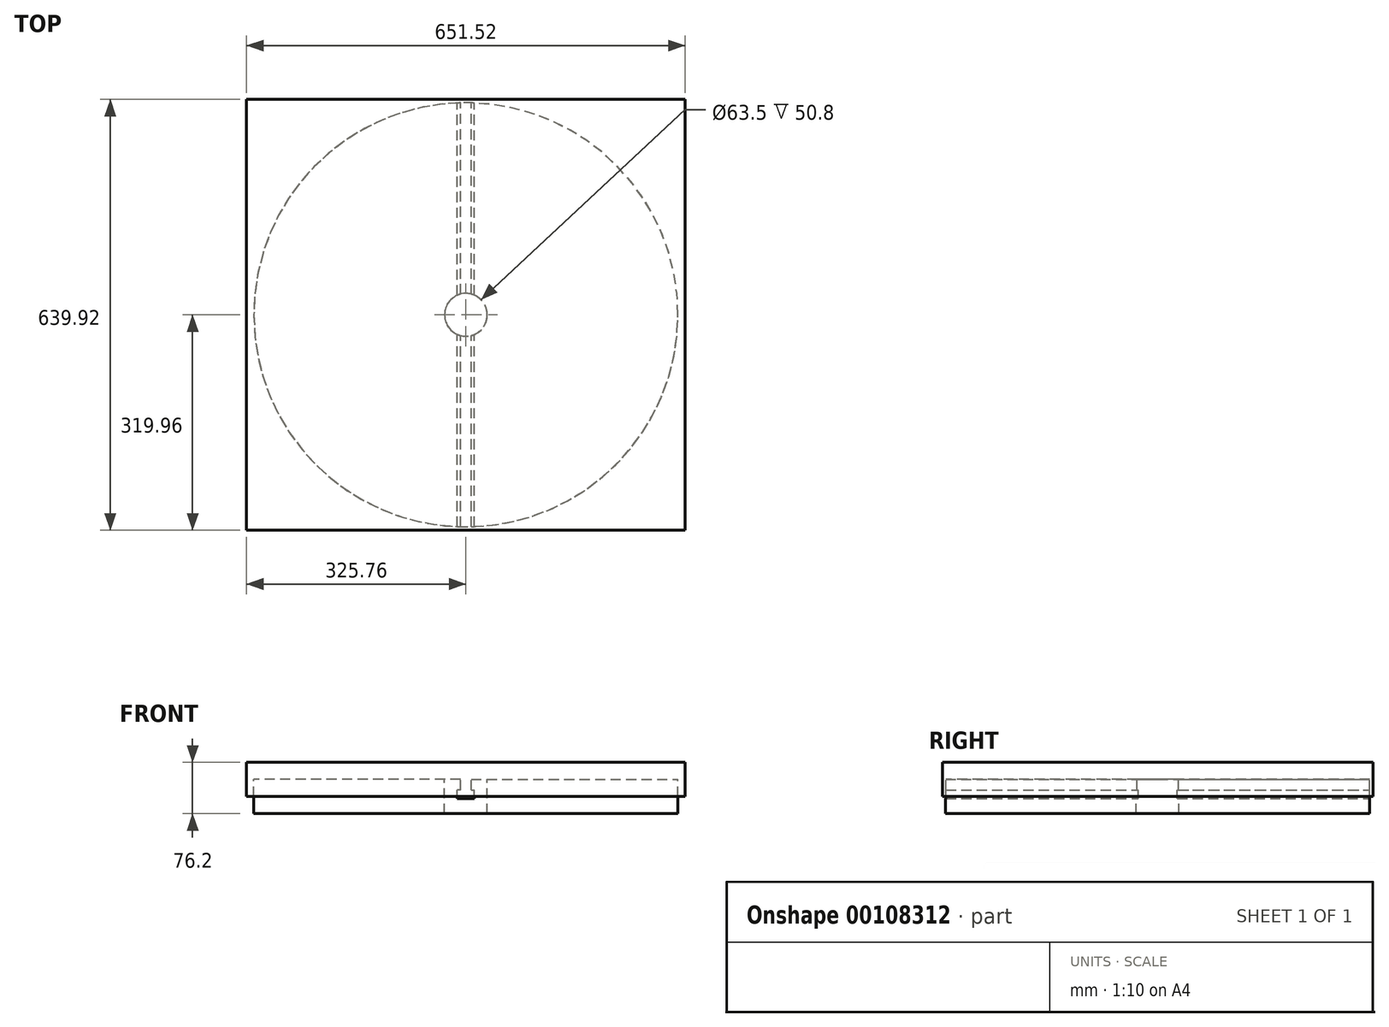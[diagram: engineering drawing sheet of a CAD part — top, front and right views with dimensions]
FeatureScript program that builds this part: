
annotation { "Feature Type Name" : "Feature", "Feature Type Description" : "" }
export const myFeature = defineFeature(function(context is Context, id is Id, definition is map)
    precondition{}
    {
        {
            var Q0;
            Q0=qCreatedBy(makeId("Top.planeOp"),FACE);
            var sketch = newSketch(context, id + "F0", { "sketchPlane" : qUnion([Q0])});
            skCircle(sketch, "E0", {"center": v(0, 0) * mm, "radius": 314.96 * mm});
            skCircle(sketch, "E1", {"center": v(0, 0) * mm, "radius": 31.75 * mm});
            skSolve(sketch);
        }
        {
            var Q0;
            Q0 = qSketchRegion(id + "F0", true);
            extrude(context, id + "F1", {"entities" : qUnion([Q0]), "oppositeDirection" : true, "depth" : 101.6 * mm, "hasSecondDirection" : true, "secondDirectionOppositeDirection" : true, "secondDirectionDepth" : 50.8 * mm});
        }
        {
            var Q0;
            Q0=qCreatedBy(makeId("Front.planeOp"),FACE);
            var sketch = newSketch(context, id + "F2", { "sketchPlane" : qUnion([Q0])});
            skLineSegment(sketch, "E2", {"start": v(0, -90) * mm, "end": v(0, -167.35) * mm, "construction": true});
            skLineSegment(sketch, "E3", {"start": v(0, -50.8) * mm, "end": v(-7.94, -50.8) * mm});
            skLineSegment(sketch, "E4", {"start": v(-7.94, -50.8) * mm, "end": v(-7.94, -66.67) * mm});
            skLineSegment(sketch, "E5", {"start": v(-7.94, -66.67) * mm, "end": v(-12.7, -66.67) * mm});
            skLineSegment(sketch, "E6", {"start": v(-12.7, -66.67) * mm, "end": v(-12.7, -79.38) * mm});
            skLineSegment(sketch, "E7", {"start": v(-12.7, -79.38) * mm, "end": v(0, -79.38) * mm});
            skLineSegment(sketch, "E8.MirrorCS", {"start": v(0, -50.8) * mm, "end": v(7.94, -50.8) * mm});
            skLineSegment(sketch, "E9.MirrorCS", {"start": v(7.94, -50.8) * mm, "end": v(7.94, -66.67) * mm});
            skLineSegment(sketch, "E10.MirrorCS", {"start": v(7.94, -66.67) * mm, "end": v(12.7, -66.67) * mm});
            skLineSegment(sketch, "E11.MirrorCS", {"start": v(12.7, -66.67) * mm, "end": v(12.7, -79.38) * mm});
            skLineSegment(sketch, "E12.MirrorCS", {"start": v(12.7, -79.38) * mm, "end": v(0, -79.38) * mm});
            skSolve(sketch);
        }
        {
            var Q0;
            Q0 = qSketchRegion(id + "F2", true);
            var Q1;
            Q1=makeQuery(id+"F1.opExtrude","SWEPT_FACE",FACE,{"disambiguationData":[OSD([sQuery(id+"F0.wireOp",EDGE,"E0")])]});
            var Q2;
            Q2=makeQuery(id+"F1.opExtrude","SWEPT_BODY",BODY,{"disambiguationData":[OSD([sQuery(id+"F0.wireOp",EDGE,"E0"),sQuery(id+"F0.wireOp",EDGE,"E1")])]});
            extrude(context, id + "F3", {"entities" : qUnion([Q0]), "operationType" : NewBodyOperationType.REMOVE, "endBound" : BoundingType.SYMMETRIC, "endBoundEntityFace" : qUnion([Q1]), "endBoundEntityBody" : qUnion([Q2]), "depth" : 629.92 * mm});
        }
        {
            var Q0;
            Q0=qCreatedBy(makeId("Top.planeOp"),FACE);
            var sketch = newSketch(context, id + "F4", { "sketchPlane" : qUnion([Q0])});
            skLineSegment(sketch, "E13.bottom", {"start": v(-325.76, 319.96) * mm, "end": v(325.76, 319.96) * mm});
            skLineSegment(sketch, "E13.top", {"start": v(-325.76, -319.96) * mm, "end": v(325.76, -319.96) * mm});
            skLineSegment(sketch, "E13.left", {"start": v(-325.76, 319.96) * mm, "end": v(-325.76, -319.96) * mm});
            skLineSegment(sketch, "E13.right", {"start": v(325.76, 319.96) * mm, "end": v(325.76, -319.96) * mm});
            skPoint(sketch, "E13.middle", {"position": v(0, 0) * mm});
            skSolve(sketch);
        }
        {
            var Q0;
            Q0=makeQuery(id+"F4.imprint","IMPRINT",FACE,{"disambiguationData":[TD([[makeQuery(id+"F4.imprint","IMPRINT",EDGE,{"derivedFrom":sQuery(id+"F4.wireOp",EDGE,"E13.bottom")}),-1.0]])]});
            extrude(context, id + "F5", {"entities" : qUnion([Q0]), "oppositeDirection" : true, "depth" : 76.2 * mm, "hasSecondDirection" : true, "secondDirectionOppositeDirection" : true, "secondDirectionDepth" : 25.4 * mm});
        }
    });
